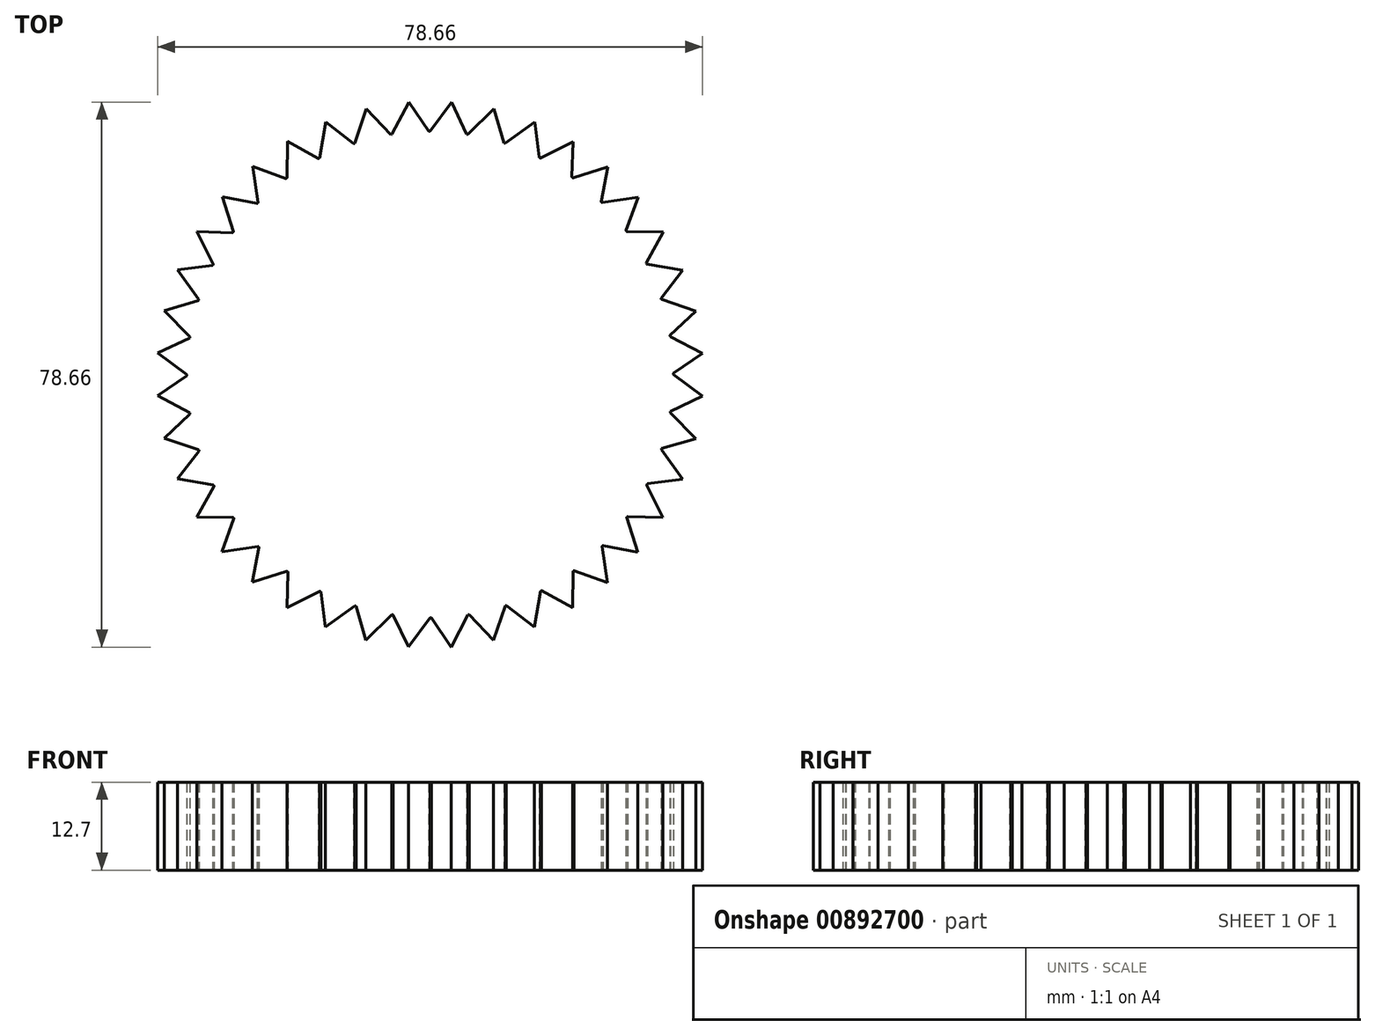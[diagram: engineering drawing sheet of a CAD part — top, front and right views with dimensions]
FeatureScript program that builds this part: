
annotation { "Feature Type Name" : "Feature", "Feature Type Description" : "" }
export const myFeature = defineFeature(function(context is Context, id is Id, definition is map)
    precondition{}
    {
        {
            var Q0;
            Q0=qCreatedBy(makeId("Top.planeOp"),FACE);
            var sketch = newSketch(context, id + "F0", { "sketchPlane" : qUnion([Q0])});
            skCircle(sketch, "E0", {"center": v(0, 0) * mm, "radius": 35.1 * mm});
            skLineSegment(sketch, "E1", {"start": v(0, 35.1) * mm, "end": v(3.13, 39.32) * mm});
            skLineSegment(sketch, "E2", {"start": v(3.13, 39.32) * mm, "end": v(5.3, 34.7) * mm});
            skLineSegment(sketch, "E3.1.0", {"start": v(-5.5, 34.67) * mm, "end": v(-3.06, 39.33) * mm});
            skLineSegment(sketch, "E3.1.1", {"start": v(-3.06, 39.33) * mm, "end": v(-0.19, 35.1) * mm});
            skLineSegment(sketch, "E3.2.0", {"start": v(-10.85, 33.38) * mm, "end": v(-9.18, 38.37) * mm});
            skLineSegment(sketch, "E3.2.1", {"start": v(-9.18, 38.37) * mm, "end": v(-5.67, 34.64) * mm});
            skLineSegment(sketch, "E3.3.0", {"start": v(-15.93, 31.27) * mm, "end": v(-15.06, 36.46) * mm});
            skLineSegment(sketch, "E3.3.1", {"start": v(-15.06, 36.46) * mm, "end": v(-11.02, 33.32) * mm});
            skLineSegment(sketch, "E3.4.0", {"start": v(-20.63, 28.4) * mm, "end": v(-20.58, 33.65) * mm});
            skLineSegment(sketch, "E3.4.1", {"start": v(-20.58, 33.65) * mm, "end": v(-16.1, 31.19) * mm});
            skLineSegment(sketch, "E3.5.0", {"start": v(-24.82, 24.82) * mm, "end": v(-25.6, 30.02) * mm});
            skLineSegment(sketch, "E3.5.1", {"start": v(-25.6, 30.02) * mm, "end": v(-20.78, 28.28) * mm});
            skLineSegment(sketch, "E3.6.0", {"start": v(-28.4, 20.63) * mm, "end": v(-29.97, 25.65) * mm});
            skLineSegment(sketch, "E3.6.1", {"start": v(-29.97, 25.65) * mm, "end": v(-24.95, 24.69) * mm});
            skLineSegment(sketch, "E3.7.0", {"start": v(-31.27, 15.93) * mm, "end": v(-33.62, 20.64) * mm});
            skLineSegment(sketch, "E3.7.1", {"start": v(-33.62, 20.64) * mm, "end": v(-28.5, 20.48) * mm});
            skLineSegment(sketch, "E3.8.0", {"start": v(-33.38, 10.85) * mm, "end": v(-36.43, 15.13) * mm});
            skLineSegment(sketch, "E3.8.1", {"start": v(-36.43, 15.13) * mm, "end": v(-31.36, 15.77) * mm});
            skLineSegment(sketch, "E3.9.0", {"start": v(-34.67, 5.5) * mm, "end": v(-38.35, 9.24) * mm});
            skLineSegment(sketch, "E3.9.1", {"start": v(-38.35, 9.24) * mm, "end": v(-33.44, 10.67) * mm});
            skLineSegment(sketch, "E3.10.0", {"start": v(-35.1, 0) * mm, "end": v(-39.32, 3.13) * mm});
            skLineSegment(sketch, "E3.10.1", {"start": v(-39.32, 3.13) * mm, "end": v(-34.7, 5.3) * mm});
            skLineSegment(sketch, "E3.11.0", {"start": v(-34.67, -5.5) * mm, "end": v(-39.33, -3.06) * mm});
            skLineSegment(sketch, "E3.11.1", {"start": v(-39.33, -3.06) * mm, "end": v(-35.1, -0.19) * mm});
            skLineSegment(sketch, "E3.12.0", {"start": v(-33.38, -10.85) * mm, "end": v(-38.37, -9.18) * mm});
            skLineSegment(sketch, "E3.12.1", {"start": v(-38.37, -9.18) * mm, "end": v(-34.64, -5.67) * mm});
            skLineSegment(sketch, "E3.13.0", {"start": v(-31.27, -15.93) * mm, "end": v(-36.46, -15.06) * mm});
            skLineSegment(sketch, "E3.13.1", {"start": v(-36.46, -15.06) * mm, "end": v(-33.32, -11.02) * mm});
            skLineSegment(sketch, "E3.14.0", {"start": v(-28.4, -20.63) * mm, "end": v(-33.65, -20.58) * mm});
            skLineSegment(sketch, "E3.14.1", {"start": v(-33.65, -20.58) * mm, "end": v(-31.19, -16.1) * mm});
            skLineSegment(sketch, "E3.15.0", {"start": v(-24.82, -24.82) * mm, "end": v(-30.02, -25.6) * mm});
            skLineSegment(sketch, "E3.15.1", {"start": v(-30.02, -25.6) * mm, "end": v(-28.28, -20.78) * mm});
            skLineSegment(sketch, "E3.16.0", {"start": v(-20.63, -28.4) * mm, "end": v(-25.65, -29.97) * mm});
            skLineSegment(sketch, "E3.16.1", {"start": v(-25.65, -29.97) * mm, "end": v(-24.69, -24.95) * mm});
            skLineSegment(sketch, "E3.17.0", {"start": v(-15.93, -31.27) * mm, "end": v(-20.64, -33.62) * mm});
            skLineSegment(sketch, "E3.17.1", {"start": v(-20.64, -33.62) * mm, "end": v(-20.48, -28.5) * mm});
            skLineSegment(sketch, "E3.18.0", {"start": v(-10.85, -33.38) * mm, "end": v(-15.13, -36.43) * mm});
            skLineSegment(sketch, "E3.18.1", {"start": v(-15.13, -36.43) * mm, "end": v(-15.77, -31.36) * mm});
            skLineSegment(sketch, "E3.19.0", {"start": v(-5.5, -34.67) * mm, "end": v(-9.24, -38.35) * mm});
            skLineSegment(sketch, "E3.19.1", {"start": v(-9.24, -38.35) * mm, "end": v(-10.67, -33.44) * mm});
            skLineSegment(sketch, "E3.20.0", {"start": v(0, -35.1) * mm, "end": v(-3.13, -39.32) * mm});
            skLineSegment(sketch, "E3.20.1", {"start": v(-3.13, -39.32) * mm, "end": v(-5.3, -34.7) * mm});
            skLineSegment(sketch, "E3.21.0", {"start": v(5.5, -34.67) * mm, "end": v(3.06, -39.33) * mm});
            skLineSegment(sketch, "E3.21.1", {"start": v(3.06, -39.33) * mm, "end": v(0.19, -35.1) * mm});
            skLineSegment(sketch, "E3.22.0", {"start": v(10.85, -33.38) * mm, "end": v(9.18, -38.37) * mm});
            skLineSegment(sketch, "E3.22.1", {"start": v(9.18, -38.37) * mm, "end": v(5.67, -34.64) * mm});
            skLineSegment(sketch, "E3.23.0", {"start": v(15.93, -31.27) * mm, "end": v(15.06, -36.46) * mm});
            skLineSegment(sketch, "E3.23.1", {"start": v(15.06, -36.46) * mm, "end": v(11.02, -33.32) * mm});
            skLineSegment(sketch, "E3.24.0", {"start": v(20.63, -28.4) * mm, "end": v(20.58, -33.65) * mm});
            skLineSegment(sketch, "E3.24.1", {"start": v(20.58, -33.65) * mm, "end": v(16.1, -31.19) * mm});
            skLineSegment(sketch, "E3.25.0", {"start": v(24.82, -24.82) * mm, "end": v(25.6, -30.02) * mm});
            skLineSegment(sketch, "E3.25.1", {"start": v(25.6, -30.02) * mm, "end": v(20.78, -28.28) * mm});
            skLineSegment(sketch, "E3.26.0", {"start": v(28.4, -20.63) * mm, "end": v(29.97, -25.65) * mm});
            skLineSegment(sketch, "E3.26.1", {"start": v(29.97, -25.65) * mm, "end": v(24.95, -24.69) * mm});
            skLineSegment(sketch, "E3.27.0", {"start": v(31.27, -15.93) * mm, "end": v(33.62, -20.64) * mm});
            skLineSegment(sketch, "E3.27.1", {"start": v(33.62, -20.64) * mm, "end": v(28.5, -20.48) * mm});
            skLineSegment(sketch, "E3.28.0", {"start": v(33.38, -10.85) * mm, "end": v(36.43, -15.13) * mm});
            skLineSegment(sketch, "E3.28.1", {"start": v(36.43, -15.13) * mm, "end": v(31.36, -15.77) * mm});
            skLineSegment(sketch, "E3.29.0", {"start": v(34.67, -5.5) * mm, "end": v(38.35, -9.24) * mm});
            skLineSegment(sketch, "E3.29.1", {"start": v(38.35, -9.24) * mm, "end": v(33.44, -10.67) * mm});
            skLineSegment(sketch, "E3.30.0", {"start": v(35.1, 0) * mm, "end": v(39.32, -3.13) * mm});
            skLineSegment(sketch, "E3.30.1", {"start": v(39.32, -3.13) * mm, "end": v(34.7, -5.3) * mm});
            skLineSegment(sketch, "E3.31.0", {"start": v(34.67, 5.5) * mm, "end": v(39.33, 3.06) * mm});
            skLineSegment(sketch, "E3.31.1", {"start": v(39.33, 3.06) * mm, "end": v(35.1, 0.19) * mm});
            skLineSegment(sketch, "E3.32.0", {"start": v(33.38, 10.85) * mm, "end": v(38.37, 9.18) * mm});
            skLineSegment(sketch, "E3.32.1", {"start": v(38.37, 9.18) * mm, "end": v(34.64, 5.67) * mm});
            skLineSegment(sketch, "E3.33.0", {"start": v(31.27, 15.93) * mm, "end": v(36.46, 15.06) * mm});
            skLineSegment(sketch, "E3.33.1", {"start": v(36.46, 15.06) * mm, "end": v(33.32, 11.02) * mm});
            skLineSegment(sketch, "E3.34.0", {"start": v(28.4, 20.63) * mm, "end": v(33.65, 20.58) * mm});
            skLineSegment(sketch, "E3.34.1", {"start": v(33.65, 20.58) * mm, "end": v(31.19, 16.1) * mm});
            skLineSegment(sketch, "E3.35.0", {"start": v(24.82, 24.82) * mm, "end": v(30.02, 25.6) * mm});
            skLineSegment(sketch, "E3.35.1", {"start": v(30.02, 25.6) * mm, "end": v(28.28, 20.78) * mm});
            skLineSegment(sketch, "E3.36.0", {"start": v(20.63, 28.4) * mm, "end": v(25.65, 29.97) * mm});
            skLineSegment(sketch, "E3.36.1", {"start": v(25.65, 29.97) * mm, "end": v(24.69, 24.95) * mm});
            skLineSegment(sketch, "E3.37.0", {"start": v(15.93, 31.27) * mm, "end": v(20.64, 33.62) * mm});
            skLineSegment(sketch, "E3.37.1", {"start": v(20.64, 33.62) * mm, "end": v(20.48, 28.5) * mm});
            skLineSegment(sketch, "E3.38.0", {"start": v(10.85, 33.38) * mm, "end": v(15.13, 36.43) * mm});
            skLineSegment(sketch, "E3.38.1", {"start": v(15.13, 36.43) * mm, "end": v(15.77, 31.36) * mm});
            skLineSegment(sketch, "E3.39.0", {"start": v(5.5, 34.67) * mm, "end": v(9.24, 38.35) * mm});
            skLineSegment(sketch, "E3.39.1", {"start": v(9.24, 38.35) * mm, "end": v(10.67, 33.44) * mm});
            skSolve(sketch);
        }
        {
            var Q0;
            Q0 = qSketchRegion(id + "F0", true);
            extrude(context, id + "F1", {"entities" : qUnion([Q0]), "depth" : 12.7 * mm, "offsetDistance" : 25.4 * mm});
        }
    });
